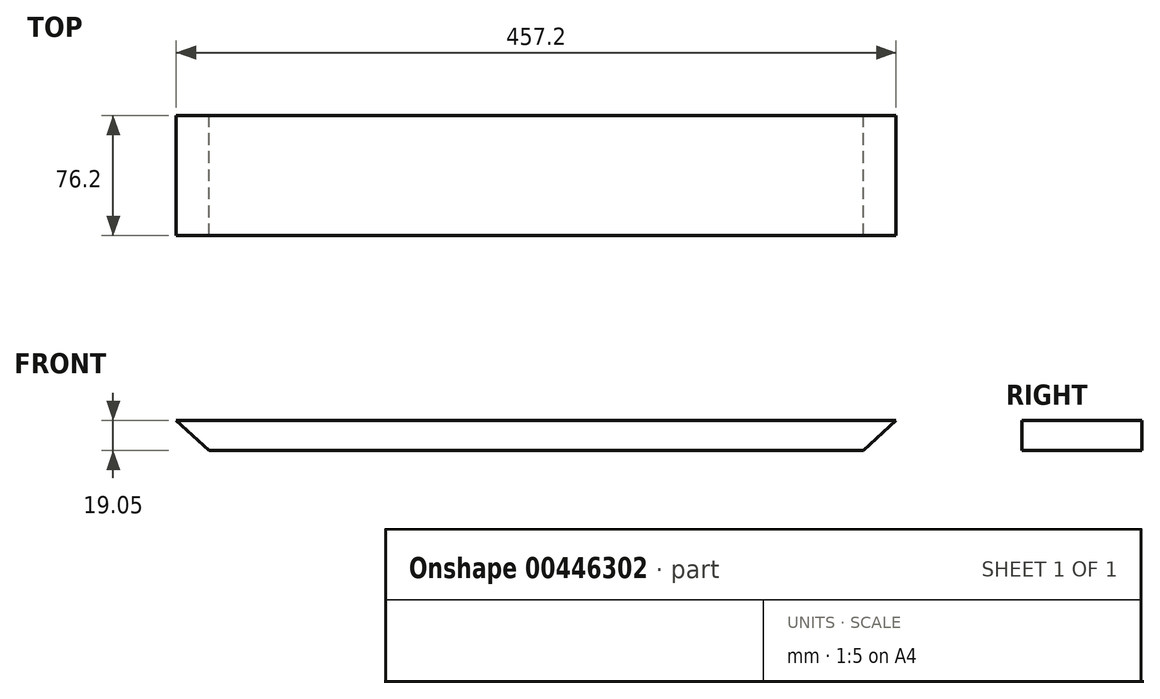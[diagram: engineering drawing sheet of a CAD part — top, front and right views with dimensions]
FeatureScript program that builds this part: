
annotation { "Feature Type Name" : "Feature", "Feature Type Description" : "" }
export const myFeature = defineFeature(function(context is Context, id is Id, definition is map)
    precondition{}
    {
        {
            var Q0;
            Q0=qCreatedBy(makeId("Front.planeOp"),FACE);
            var sketch = newSketch(context, id + "F0", { "sketchPlane" : qUnion([Q0])});
            skLineSegment(sketch, "E0", {"start": v(0, 0) * mm, "end": v(457.2, 0) * mm});
            skLineSegment(sketch, "E1", {"start": v(457.2, 0) * mm, "end": v(436.41, -19.05) * mm});
            skLineSegment(sketch, "E2", {"start": v(436.41, -19.05) * mm, "end": v(20.79, -19.05) * mm});
            skLineSegment(sketch, "E3", {"start": v(20.79, -19.05) * mm, "end": v(0, 0) * mm});
            skSolve(sketch);
        }
        {
            var Q0;
            Q0=makeQuery(id+"F0.imprint","IMPRINT",FACE,{"disambiguationData":[TD([[makeQuery(id+"F0.imprint","IMPRINT",EDGE,{"derivedFrom":sQuery(id+"F0.wireOp",EDGE,"E0")}),-1.0]])]});
            extrude(context, id + "F1", {"entities" : qUnion([Q0]), "depth" : 76.2 * mm});
        }
    });
